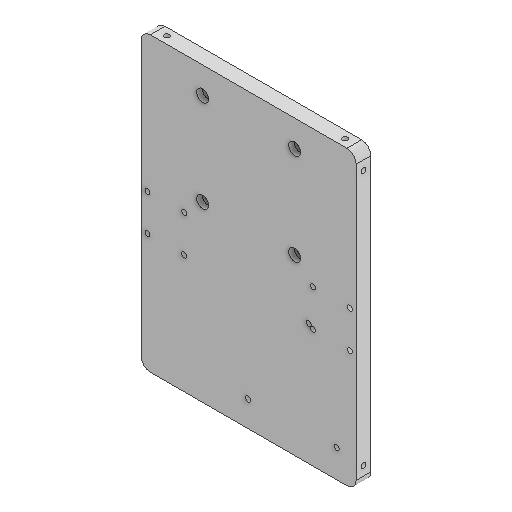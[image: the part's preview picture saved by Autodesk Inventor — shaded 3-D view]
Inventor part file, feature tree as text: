
AUTODESK INVENTOR PART (.ipt)
format: ipt  version: 2022 (Build 260153000, 153)  size: 206,848 bytes
history: native  units: mm
features: sketch x9, reference x9, extrude x5, projected_geometry x5, other x4, hole x3, plane x2
ambient origin geometry x8: Origin, YZ Plane, XZ Plane, XY Plane, X Axis, Y Axis, Z Axis, Center Point
bodies: Volumenkörper1 (feature_tree)
feature tree (37):
  plane  "Arbeitsebene1"
  sketch  "Skizze1"  dims[d1=0.0mm d13=20.0mm]
  plane  "Arbeitsebene2"
  extrude  "Extrusion1"  Depth=20.0mm
  hole  "Bohrung1"  [1 undecoded]
  hole  "Bohrung2"  [1 undecoded]
  extrude  "Extrusion3"  Depth=5.0mm
  extrude  "Extrusion4"  Depth=10.0mm TaperAngle=0.0deg
  extrude  "Extrusion5"  Depth=2.8mm
  extrude  "Extrusion6"  Depth=5.0mm
  hole  "Bohrung3"  [1 undecoded]
  sketch  "Skizze2"  dims[d14=20.0mm d15=20.0mm]
  reference  "Referenz1"
  reference  "Referenz2"
  reference  "Referenz3"
  reference  "Referenz4"
  reference  "Referenz5"
  sketch  "Skizze4"  dims[d16=20.0mm]
  projected_geometry  "Projizierte Kontur2"
  sketch  "Skizze5"  dims[d21=2.8mm d22=6.0mm d23=7.0mm d24=10.0mm d25=90.0deg d26=8.0mm d27=20.594885mm]
  reference  "Referenz6"
  sketch  "Skizze6"  dims[d28=2.8mm d29=6.0mm d30=6.5mm d31=3.0mm d32=90.0deg d33=8.0mm d34=20.594885mm d52=2.8mm]
  projected_geometry  "Projizierte Kontur3"
  sketch  "Skizze7"  dims[d53=2.8mm d54=5.0mm]
  projected_geometry  "Projizierte Kontur4"
  sketch  "Skizze8"  dims[d55=5.0mm d56=10.0mm d57=0.0mm]
  projected_geometry  "Projizierte Kontur5"
  sketch  "Skizze9"  dims[d58=2.8mm d59=2.8mm]
  projected_geometry  "Projizierte Kontur6"
  sketch  "Skizze10"  dims[d60=5.0mm d61=5.0mm d62=10.0mm d63=0.0mm d64=10.0mm d65=0.0mm d66=10.0mm d67=0.0mm d68=4.0mm d69=0.0mm d70=4.0mm d71=4.0mm d72=2.8mm d73=6.0mm d74=6.5mm d75=4.0mm d76=90.0deg d77=8.0mm d78=20.594885mm]
  reference  "Referenz9"
  reference  "Referenz10"
  reference  "Referenz11"
  other  "Omnicscope_Xiao.iam"
  other  "Omniscope_USBC_Wellplatemount2:1"
  other  "00_linear_z_stage_60mm:1"
  other  "00_Arduino_CNC_Assembly:1"
note: 3 required parameter values undecoded (feature->parameter linkage not recoverable at this tier; creation-order binding heuristic only, values carry confidence <= 0.55)
